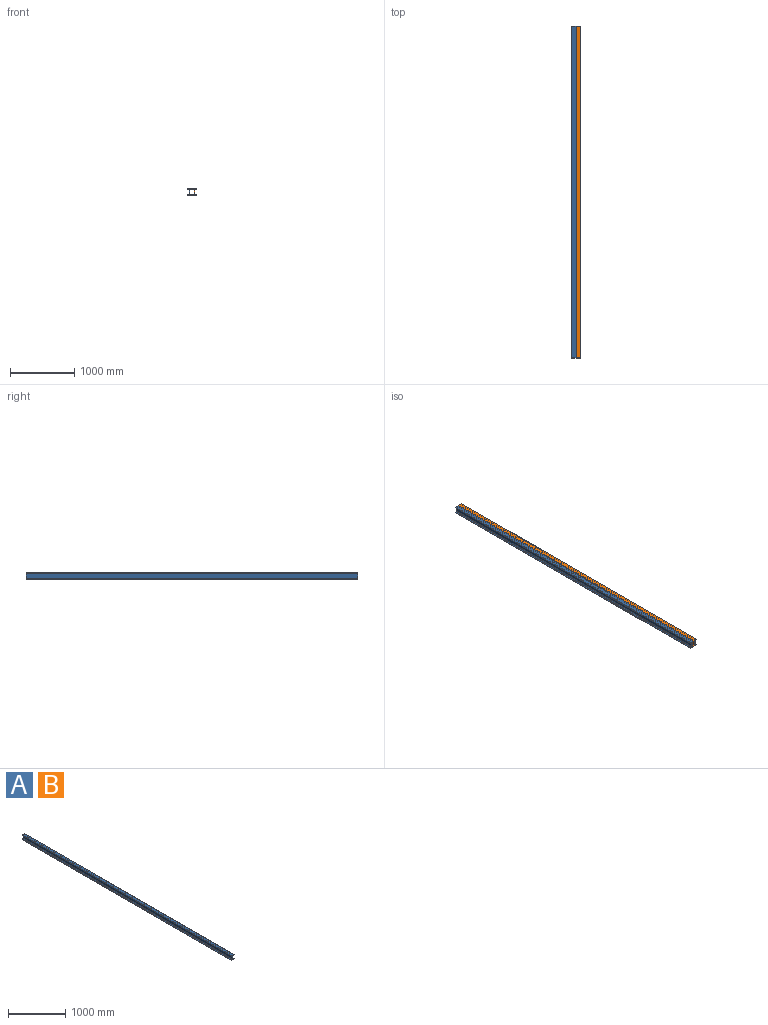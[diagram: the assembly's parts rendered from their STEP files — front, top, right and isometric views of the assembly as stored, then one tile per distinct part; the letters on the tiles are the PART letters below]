
ASSEMBLY  parts=2 mates=1
PART A: 22 faces, bbox 71.1x5181.6x101.6 mm
  f0: plane 101.6x71.12mm, normal (0,-1,0), area 1834.7mm2, adj f2,f3,f4,f5,f6,f7,f8,f9
  f1: plane 101.6x71.12mm, normal (0,1,0), area 1834.7mm2, adj f2,f3,f4,f5,f6,f7,f8,f9
  f2: plane 5181.6x20.42mm, normal (0.17,0,-0.98), area 107418.3mm2, adj f0,f1,f3,f21
  f3: cylinder r=10.53mm len=5181.6mm, axis (0,1,0), area 76201.3mm2, adj f0,f1,f2,f4
  f4: plane 5181.6x63.5mm, normal (1,0,0), area 329031.6mm2, adj f0,f1,f3,f5
  f5: cylinder r=10.53mm len=5181.6mm, axis (0,1,0), area 76201.3mm2, adj f0,f1,f4,f6
  f6: plane 5181.6x20.42mm, normal (0.17,0,0.98), area 107418.3mm2, adj f0,f1,f5,f7
  f7: cylinder r=2.81mm len=5181.6mm, axis (0,1,0), area 20102.8mm2, adj f0,f1,f6,f8
  f8: plane 5181.6x2.34mm, normal (1,0,0), area 12104.4mm2, adj f0,f1,f7,f9
  f9: plane 5181.6x71.12mm, normal (0,0,-1), area 368515.4mm2, adj f0,f1,f8,f10
  f10: plane 5181.6x2.34mm, normal (-1,0,0), area 12104.4mm2, adj f0,f1,f9,f11
  f11: cylinder r=2.81mm len=5181.6mm, axis (0,1,0), area 20102.8mm2, adj f0,f1,f10,f12
  f12: plane 5181.6x20.42mm, normal (-0.17,0,0.98), area 107418.3mm2, adj f0,f1,f11,f13
  f13: cylinder r=10.53mm len=5181.6mm, axis (0,1,0), area 76201.3mm2, adj f0,f1,f12,f14
  f14: plane 5181.6x63.5mm, normal (-1,0,0), area 329031.6mm2, adj f0,f1,f13,f15
  f15: cylinder r=10.53mm len=5181.6mm, axis (0,1,0), area 76201.3mm2, adj f0,f1,f14,f16
  f16: plane 5181.6x20.42mm, normal (-0.17,0,-0.98), area 107418.3mm2, adj f0,f1,f15,f17
  f17: cylinder r=2.81mm len=5181.6mm, axis (0,1,0), area 20102.8mm2, adj f0,f1,f16,f18
  f18: plane 5181.6x2.34mm, normal (-1,0,0), area 12104.4mm2, adj f0,f1,f17,f19
  f19: plane 5181.6x71.12mm, normal (0,0,1), area 368515.4mm2, adj f0,f1,f18,f20
  f20: plane 5181.6x2.34mm, normal (1,0,0), area 12104.4mm2, adj f0,f1,f19,f21
  f21: cylinder r=2.81mm len=5181.6mm, axis (0,1,0), area 20102.8mm2, adj f0,f1,f2,f20
PART B: same geometry as A
PLACE A at identity
PLACE B t=(71.12,0,0)mm
MATE fastened A.f20 <-> B.f18  axis (1,0,0) through (35.56,0,50.8)mm
